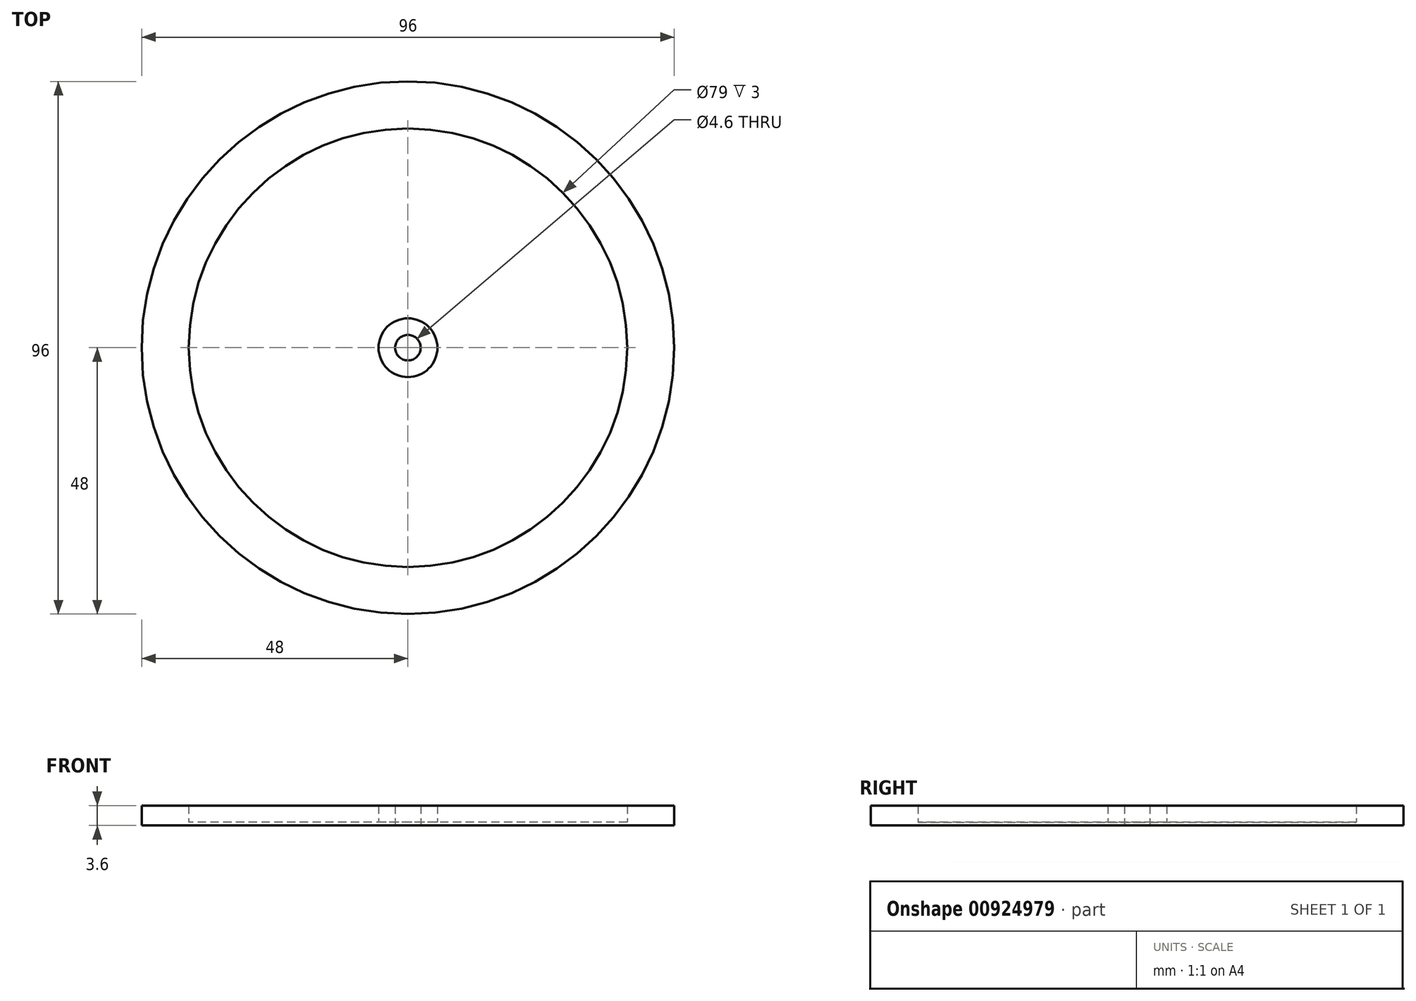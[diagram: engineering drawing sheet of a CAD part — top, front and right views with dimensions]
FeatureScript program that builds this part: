
annotation { "Feature Type Name" : "Feature", "Feature Type Description" : "" }
export const myFeature = defineFeature(function(context is Context, id is Id, definition is map)
    precondition{}
    {
        {
            var Q0;
            Q0=qCreatedBy(makeId("Top.planeOp"),FACE);
            var sketch = newSketch(context, id + "F0", { "sketchPlane" : qUnion([Q0])});
            skCircle(sketch, "E0", {"center": v(0, 0) * mm, "radius": 39.5 * mm});
            skCircle(sketch, "E1", {"center": v(0, 0) * mm, "radius": 48 * mm});
            skCircle(sketch, "E2", {"center": v(0, 0) * mm, "radius": 2.3 * mm});
            skCircle(sketch, "E3", {"center": v(0, 0) * mm, "radius": 5.3 * mm});
            skSolve(sketch);
        }
        {
            var Q0;
            Q0 = qSketchRegion(id + "F0", true);
            var Q1;
            Q1=makeQuery(id+"F0.imprint","IMPRINT",FACE,{"disambiguationData":[TD([[makeQuery(id+"F0.imprint","IMPRINT",EDGE,{"derivedFrom":sQuery(id+"F0.wireOp",EDGE,"E2")}),-1.0]])]});
            extrude(context, id + "F1", {"entities" : qUnion([Q0, Q1]), "depth" : 3 * mm, "offsetDistance" : 25 * mm});
        }
        {
            var Q0;
            Q0 = qSketchRegion(id + "F0", true);
            var Q1;
            Q1=makeQuery(id+"F0.imprint","IMPRINT",FACE,{"disambiguationData":[TD([[makeQuery(id+"F0.imprint","IMPRINT",EDGE,{"derivedFrom":sQuery(id+"F0.wireOp",EDGE,"E0")}),1.0]])]});
            var Q2;
            Q2=makeQuery(id+"F0.imprint","IMPRINT",FACE,{"disambiguationData":[TD([[makeQuery(id+"F0.imprint","IMPRINT",EDGE,{"derivedFrom":sQuery(id+"F0.wireOp",EDGE,"E2")}),-1.0]])]});
            extrude(context, id + "F2", {"entities" : qUnion([Q0, Q1, Q2]), "operationType" : NewBodyOperationType.ADD, "oppositeDirection" : true, "depth" : 0.6 * mm, "offsetDistance" : 25 * mm});
        }
    });
